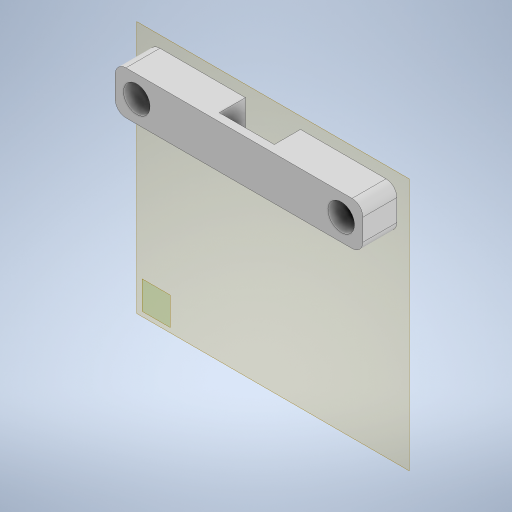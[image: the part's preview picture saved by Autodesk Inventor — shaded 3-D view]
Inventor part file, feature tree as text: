
AUTODESK INVENTOR PART (.ipt)
format: ipt  version: 2023 (Build 270158000, 158)  size: 282,112 bytes
history: native  units: mm
features: reference x6, other x4, extrude x3, sketch x3, plane x2, projected_geometry x1
ambient origin geometry x8: Origin, YZ Plane, XZ Plane, XY Plane, X Axis, Y Axis, Z Axis, Center Point
bodies: Solid1 (feature_tree)
feature tree (19):
  plane  "Work Plane1"
  extrude  "Extrusion1"  Depth=7.842mm
  extrude  "Extrusion2"  Depth=0.2mm
  plane  "Work Plane2"
  extrude  "Extrusion3"  Depth=12.908mm TaperAngle=0.0deg
  sketch  "Sketch1"  dims[d0=7.842mm d1=0.0mm d2=0.1mm]
  reference  "Reference1"
  reference  "Reference2"
  reference  "Reference3"
  sketch  "Sketch2"  dims[d3=0.1mm d4=0.2mm]
  sketch  "Sketch3"  dims[d5=12.908mm d6=0.0mm d7=12.908mm d8=0.0mm]
  projected_geometry  "Projected Loop1"
  reference  "Reference4"
  reference  "Reference5"
  reference  "Reference6"
  parser-record x1  (decoder bookkeeping rows leaked as tree rows — omitted from the tree; the rows remain in map.json)
  other  "Assembly_V6.iam"
  other  "house_V6:1"
  other  "longerScrew:1"
note: 1 file-system path scrubbed to <path> (originals preserved in map.json)
